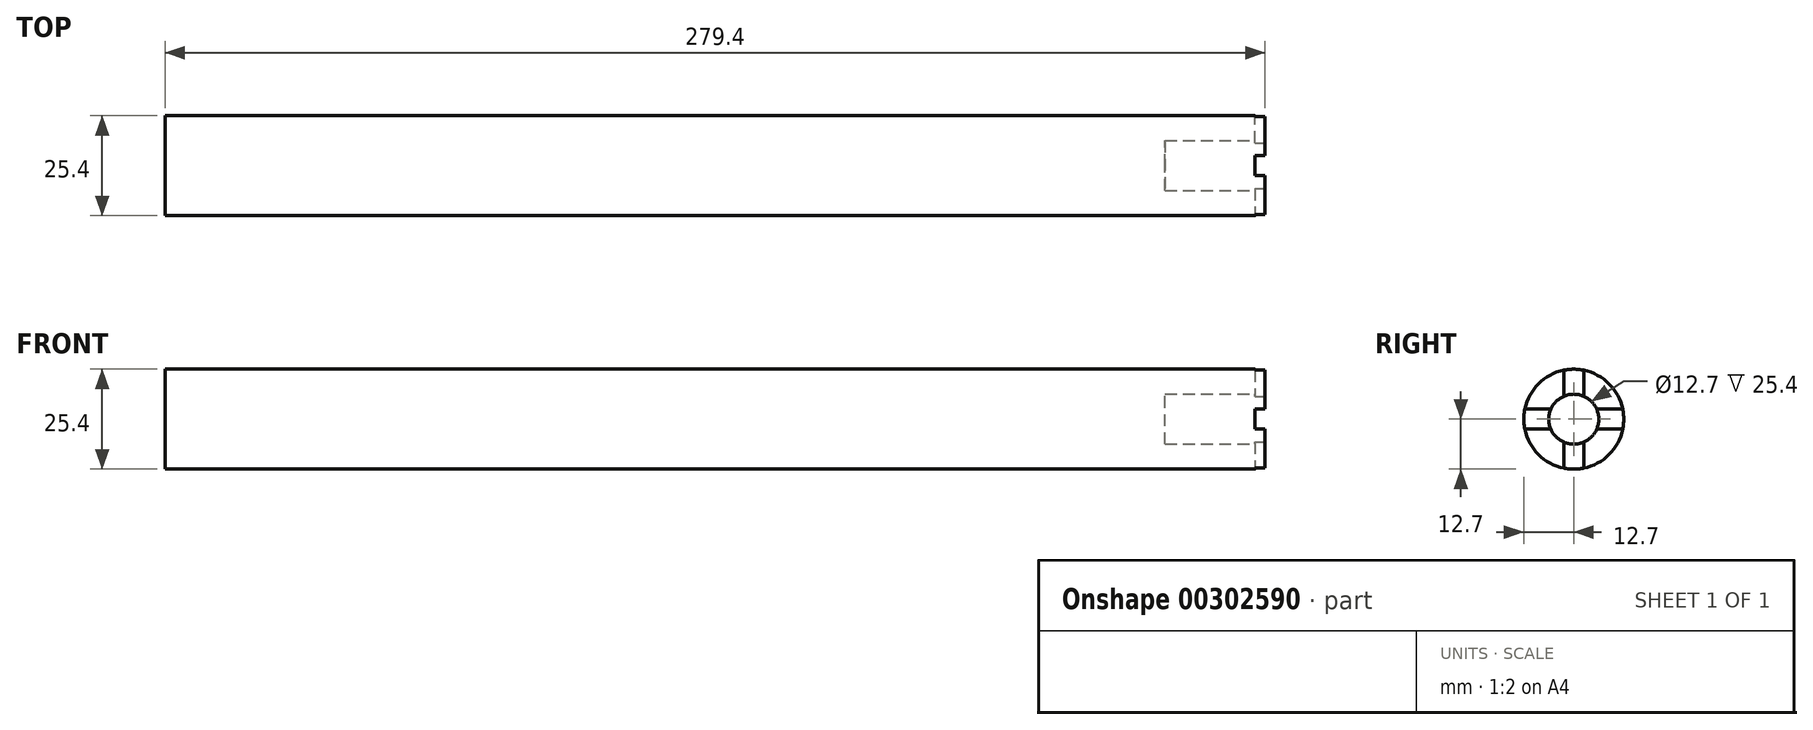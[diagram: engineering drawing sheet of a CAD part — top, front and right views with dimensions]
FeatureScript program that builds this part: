
annotation { "Feature Type Name" : "Feature", "Feature Type Description" : "" }
export const myFeature = defineFeature(function(context is Context, id is Id, definition is map)
    precondition{}
    {
        {
            var Q0;
            Q0=qCreatedBy(makeId("Right.planeOp"),FACE);
            var sketch = newSketch(context, id + "F0", { "sketchPlane" : qUnion([Q0])});
            skCircle(sketch, "E0", {"center": v(0, 0) * mm, "radius": 12.7 * mm});
            skSolve(sketch);
        }
        {
            var Q0;
            Q0=makeQuery(id+"F0.imprint","IMPRINT",FACE,{"disambiguationData":[TD([[makeQuery(id+"F0.imprint","IMPRINT",EDGE,{"derivedFrom":sQuery(id+"F0.wireOp",EDGE,"E0")}),1.0]])]});
            extrude(context, id + "F1", {"entities" : qUnion([Q0]), "oppositeDirection" : true, "depth" : 279.4 * mm});
        }
        {
            var Q0;
            Q0=makeQuery(id+"F1.opExtrude","CAP_FACE",FACE,{"disambiguationData":[OSD([sQuery(id+"F0.wireOp",EDGE,"E0")])],"isStart":true});
            var sketch = newSketch(context, id + "F2", { "sketchPlane" : qUnion([Q0])});
            skCircle(sketch, "E1", {"center": v(0, 0) * mm, "radius": 6.35 * mm});
            skSolve(sketch);
        }
        {
            var Q0;
            Q0=makeQuery(id+"F2.imprint","IMPRINT",FACE,{"disambiguationData":[TD([[makeQuery(id+"F2.imprint","IMPRINT",EDGE,{"derivedFrom":sQuery(id+"F2.wireOp",EDGE,"E1")}),1.0]])]});
            extrude(context, id + "F3", {"entities" : qUnion([Q0]), "operationType" : NewBodyOperationType.REMOVE, "oppositeDirection" : true, "depth" : 25.4 * mm});
        }
        {
            var Q0;
            Q0=qCreatedBy(makeId("Right.planeOp"),FACE);
            var sketch = newSketch(context, id + "F4", { "sketchPlane" : qUnion([Q0])});
            skLineSegment(sketch, "E2", {"start": v(-2.54, 12.44) * mm, "end": v(-2.54, 5.82) * mm});
            skLineSegment(sketch, "E3", {"start": v(2.54, 12.44) * mm, "end": v(2.54, 5.82) * mm});
            skLineSegment(sketch, "E4", {"start": v(5.82, 2.54) * mm, "end": v(12.44, 2.54) * mm});
            skLineSegment(sketch, "E5", {"start": v(5.82, -2.54) * mm, "end": v(12.44, -2.54) * mm});
            skLineSegment(sketch, "E6", {"start": v(2.54, -5.82) * mm, "end": v(2.54, -12.44) * mm});
            skLineSegment(sketch, "E7", {"start": v(-2.54, -5.82) * mm, "end": v(-2.54, -12.44) * mm});
            skLineSegment(sketch, "E8", {"start": v(-5.82, 2.54) * mm, "end": v(-12.44, 2.54) * mm});
            skLineSegment(sketch, "E9", {"start": v(-12.44, -2.54) * mm, "end": v(-5.82, -2.54) * mm});
            skLineSegment(sketch, "E10", {"start": v(-14.17, 0) * mm, "end": v(16.48, 0) * mm, "construction": true});
            skLineSegment(sketch, "E11", {"start": v(0, 17.24) * mm, "end": v(0, -14.73) * mm, "construction": true});
            skArc(sketch, "E12", {"start": v(-5.82, 2.54) * mm, "mid": v(-6.35, 0) * mm, "end": v(-5.82, -2.54) * mm});
            skArc(sketch, "E13", {"start": v(-12.44, 2.54) * mm, "mid": v(-12.7, 0) * mm, "end": v(-12.44, -2.54) * mm});
            skArc(sketch, "E14", {"start": v(-2.54, -12.44) * mm, "mid": v(0, -12.7) * mm, "end": v(2.54, -12.44) * mm});
            skArc(sketch, "E15", {"start": v(12.44, -2.54) * mm, "mid": v(12.7, 0) * mm, "end": v(12.44, 2.54) * mm});
            skArc(sketch, "E16", {"start": v(2.54, 12.44) * mm, "mid": v(0, 12.7) * mm, "end": v(-2.54, 12.44) * mm});
            skArc(sketch, "E17", {"start": v(-2.54, 5.82) * mm, "mid": v(0, -6.35) * mm, "end": v(2.54, 5.82) * mm});
            skArc(sketch, "E18", {"start": v(-2.54, -5.82) * mm, "mid": v(0, -6.35) * mm, "end": v(2.54, -5.82) * mm});
            skArc(sketch, "E19", {"start": v(5.82, -2.54) * mm, "mid": v(6.35, 0) * mm, "end": v(5.82, 2.54) * mm});
            skSolve(sketch);
        }
        {
            var Q0;
            Q0=makeQuery(id+"F4.imprint","IMPRINT",FACE,{"disambiguationData":[TD([[makeQuery(id+"F4.imprint","IMPRINT",EDGE,{"derivedFrom":sQuery(id+"F4.wireOp",EDGE,"E6")}),-1.0]])]});
            var Q1;
            {var subQ0=sQuery(id+"F4.wireOp",EDGE,"E8");Q1=makeQuery(id+"F4.imprint","IMPRINT",FACE,{"disambiguationData":[TD([[makeQuery(id+"F4.imprint","IMPRINT",EDGE,{"derivedFrom":subQ0}),1.0]])]});}
            var Q2;
            {var subQ1=sQuery(id+"F4.wireOp",EDGE,"E2");Q2=makeQuery(id+"F4.imprint","IMPRINT",FACE,{"disambiguationData":[TD([[makeQuery(id+"F4.imprint","IMPRINT",EDGE,{"derivedFrom":subQ1}),1.0]])]});}
            var Q3;
            Q3=makeQuery(id+"F4.imprint","IMPRINT",FACE,{"disambiguationData":[TD([[makeQuery(id+"F4.imprint","IMPRINT",EDGE,{"derivedFrom":sQuery(id+"F4.wireOp",EDGE,"E4")}),-1.0]])]});
            extrude(context, id + "F5", {"entities" : qUnion([Q0, Q1, Q2, Q3]), "operationType" : NewBodyOperationType.REMOVE, "oppositeDirection" : true, "depth" : 2.54 * mm});
        }
    });
